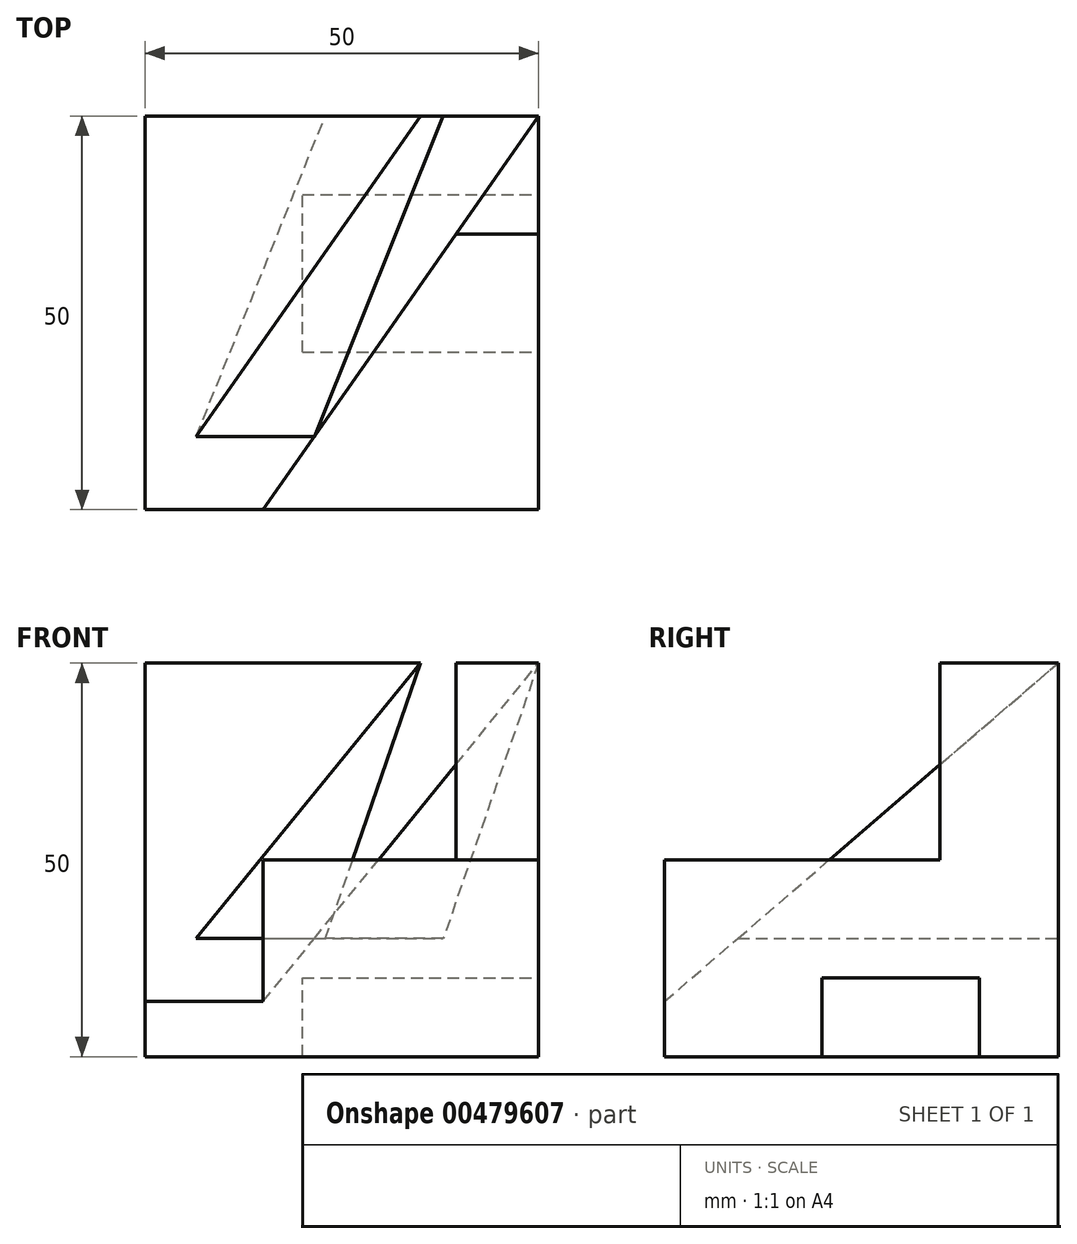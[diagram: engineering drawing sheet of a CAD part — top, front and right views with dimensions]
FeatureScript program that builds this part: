
annotation { "Feature Type Name" : "Feature", "Feature Type Description" : "" }
export const myFeature = defineFeature(function(context is Context, id is Id, definition is map)
    precondition{}
    {
        {
            var Q0;
            Q0=qCreatedBy(makeId("Top.planeOp"),FACE);
            var sketch = newSketch(context, id + "F0", { "sketchPlane" : qUnion([Q0])});
            skLineSegment(sketch, "E0.bottom", {"start": v(0, 0) * mm, "end": v(50, 0) * mm});
            skLineSegment(sketch, "E0.top", {"start": v(0, 50) * mm, "end": v(50, 50) * mm});
            skLineSegment(sketch, "E0.left", {"start": v(0, 0) * mm, "end": v(0, 50) * mm});
            skLineSegment(sketch, "E0.right", {"start": v(50, 0) * mm, "end": v(50, 50) * mm});
            skSolve(sketch);
        }
        {
            var Q0;
            Q0 = qSketchRegion(id + "F0", true);
            extrude(context, id + "F1", {"entities" : qUnion([Q0]), "depth" : 50 * mm});
        }
        {
            var Q0;
            Q0=makeQuery(id+"F1.opExtrude","SWEPT_FACE",FACE,{"disambiguationData":[OSD([sQuery(id+"F0.wireOp",EDGE,"E0.left")])]});
            cPlane(context, id + "F2", {"entities" : qUnion([Q0]), "cplaneType" : CPlaneType.OFFSET, "offset" : 20 * mm, "oppositeDirection" : true, "width" : 150 * mm, "height" : 150 * mm});
        }
        {
            var Q0;
            Q0=makeQuery(id+"F1.opExtrude","SWEPT_FACE",FACE,{"disambiguationData":[OSD([sQuery(id+"F0.wireOp",EDGE,"E0.right")])]});
            var sketch = newSketch(context, id + "F3", { "sketchPlane" : qUnion([Q0])});
            skLineSegment(sketch, "E1.bottom", {"start": v(20, 0) * mm, "end": v(40, 0) * mm});
            skLineSegment(sketch, "E1.top", {"start": v(20, 10) * mm, "end": v(40, 10) * mm});
            skLineSegment(sketch, "E1.left", {"start": v(20, 0) * mm, "end": v(20, 10) * mm});
            skLineSegment(sketch, "E1.right", {"start": v(40, 0) * mm, "end": v(40, 10) * mm});
            skSolve(sketch);
        }
        {
            var Q0;
            Q0 = qSketchRegion(id + "F3", true);
            var Q1;
            Q1=qCreatedBy(id+"F2.planeOp",FACE);
            extrude(context, id + "F4", {"entities" : qUnion([Q0]), "operationType" : NewBodyOperationType.REMOVE, "endBound" : BoundingType.UP_TO_SURFACE, "oppositeDirection" : true, "endBoundEntityFace" : qUnion([Q1]), "depth" : 25 * mm});
        }
        {
            var Q0;
            Q0=makeQuery(id+"F1.opExtrude","CAP_FACE",FACE,{"disambiguationData":[OSD([sQuery(id+"F0.wireOp",EDGE,"E0.bottom"),sQuery(id+"F0.wireOp",EDGE,"E0.top"),sQuery(id+"F0.wireOp",EDGE,"E0.left"),sQuery(id+"F0.wireOp",EDGE,"E0.right")])],"isStart":true});
            cPlane(context, id + "F5", {"entities" : qUnion([Q0]), "cplaneType" : CPlaneType.OFFSET, "offset" : 25 * mm, "oppositeDirection" : true, "width" : 150 * mm, "height" : 150 * mm});
        }
        {
            var Q0;
            Q0=makeQuery(id+"F1.opExtrude","CAP_FACE",FACE,{"disambiguationData":[OSD([sQuery(id+"F0.wireOp",EDGE,"E0.bottom"),sQuery(id+"F0.wireOp",EDGE,"E0.top"),sQuery(id+"F0.wireOp",EDGE,"E0.left"),sQuery(id+"F0.wireOp",EDGE,"E0.right")])],"isStart":false});
            var sketch = newSketch(context, id + "F6", { "sketchPlane" : qUnion([Q0])});
            skLineSegment(sketch, "E2", {"start": v(50, 0) * mm, "end": v(15, 0) * mm});
            skLineSegment(sketch, "E3", {"start": v(15, 0) * mm, "end": v(50, 50) * mm});
            skLineSegment(sketch, "E4", {"start": v(50, 50) * mm, "end": v(50, 0) * mm});
            skLineSegment(sketch, "E5", {"start": v(50, 0) * mm, "end": v(50, 35) * mm});
            skLineSegment(sketch, "E6", {"start": v(50, 35) * mm, "end": v(39.5, 35) * mm});
            skSolve(sketch);
        }
        {
            var Q0;
            {var subQ0=sQuery(id+"F6.wireOp",EDGE,"E2");Q0=makeQuery(id+"F6.imprint","IMPRINT",FACE,{"disambiguationData":[TD([[makeQuery(id+"F6.imprint","IMPRINT",EDGE,{"derivedFrom":subQ0}),1.0]])]});}
            var Q1;
            Q1=qCreatedBy(id+"F5.planeOp",FACE);
            extrude(context, id + "F7", {"entities" : qUnion([Q0]), "operationType" : NewBodyOperationType.REMOVE, "endBound" : BoundingType.UP_TO_SURFACE, "oppositeDirection" : true, "endBoundEntityFace" : qUnion([Q1]), "depth" : 25 * mm});
        }
        {
            var Q0;
            Q0=makeQuery(id+"F1.opExtrude","SWEPT_FACE",FACE,{"disambiguationData":[OSD([sQuery(id+"F0.wireOp",EDGE,"E0.left")])]});
            var sketch = newSketch(context, id + "F8", { "sketchPlane" : qUnion([Q0])});
            skLineSegment(sketch, "E7", {"start": v(0, 0) * mm, "end": v(0, 7) * mm});
            skLineSegment(sketch, "E8", {"start": v(0, 7) * mm, "end": v(-50, 50) * mm});
            skSolve(sketch);
        }
        {
            var Q0;
            {var subQ0=sQuery(id+"F8.wireOp",EDGE,"E8");Q0=makeQuery(id+"F8.imprint","IMPRINT",FACE,{"disambiguationData":[TD([[makeQuery(id+"F8.imprint","IMPRINT",EDGE,{"derivedFrom":subQ0}),-1.0]])]});}
            var Q1;
            Q1=makeQuery(id+"F7.boolean.opBoolean","COPY",FACE,{"derivedFrom":makeQuery(id+"F7.opExtrude","SWEPT_FACE",FACE,{"disambiguationData":[OSD([sQuery(id+"F6.wireOp",EDGE,"E3")])]})});
            extrude(context, id + "F9", {"entities" : qUnion([Q0]), "operationType" : NewBodyOperationType.REMOVE, "endBound" : BoundingType.UP_TO_SURFACE, "oppositeDirection" : true, "depth" : 25 * mm, "endBoundEntityFace" : qUnion([Q1]), "offsetDistance" : 25 * mm});
        }
        {
            var Q0;
            Q0=makeQuery(id+"F1.opExtrude","CAP_FACE",FACE,{"disambiguationData":[OSD([sQuery(id+"F0.wireOp",EDGE,"E0.bottom"),sQuery(id+"F0.wireOp",EDGE,"E0.top"),sQuery(id+"F0.wireOp",EDGE,"E0.left"),sQuery(id+"F0.wireOp",EDGE,"E0.right")])],"isStart":true});
            cPlane(context, id + "F10", {"entities" : qUnion([Q0]), "cplaneType" : CPlaneType.OFFSET, "offset" : 15 * mm, "oppositeDirection" : true, "width" : 150 * mm, "height" : 150 * mm});
        }
        {
            var Q0;
            Q0=makeQuery(id+"F9.boolean.opBoolean","COPY",FACE,{"derivedFrom":makeQuery(id+"F9.opExtrude","SWEPT_FACE",FACE,{"disambiguationData":[OSD([sQuery(id+"F8.wireOp",EDGE,"E8")])]})});
            var sketch = newSketch(context, id + "F11", { "sketchPlane" : qUnion([Q0])});
            skLineSegment(sketch, "E9", {"start": v(50, 70.51) * mm, "end": v(15, 4.56) * mm});
            skLineSegment(sketch, "E10", {"start": v(15, 4.56) * mm, "end": v(0, 4.56) * mm});
            skLineSegment(sketch, "E11", {"start": v(0, 4.56) * mm, "end": v(35, 70.51) * mm});
            skLineSegment(sketch, "E12", {"start": v(35, 70.51) * mm, "end": v(50, 70.51) * mm});
            skSolve(sketch);
        }
        {
            var Q0;
            Q0 = qSketchRegion(id + "F11", true);
            var Q1;
            Q1=qCreatedBy(id+"F10.planeOp",FACE);
            extrude(context, id + "F12", {"entities" : qUnion([Q0]), "operationType" : NewBodyOperationType.REMOVE, "endBound" : BoundingType.UP_TO_SURFACE, "oppositeDirection" : true, "depth" : 25 * mm, "endBoundEntityFace" : qUnion([Q1]), "offsetDistance" : 25 * mm});
        }
    });
